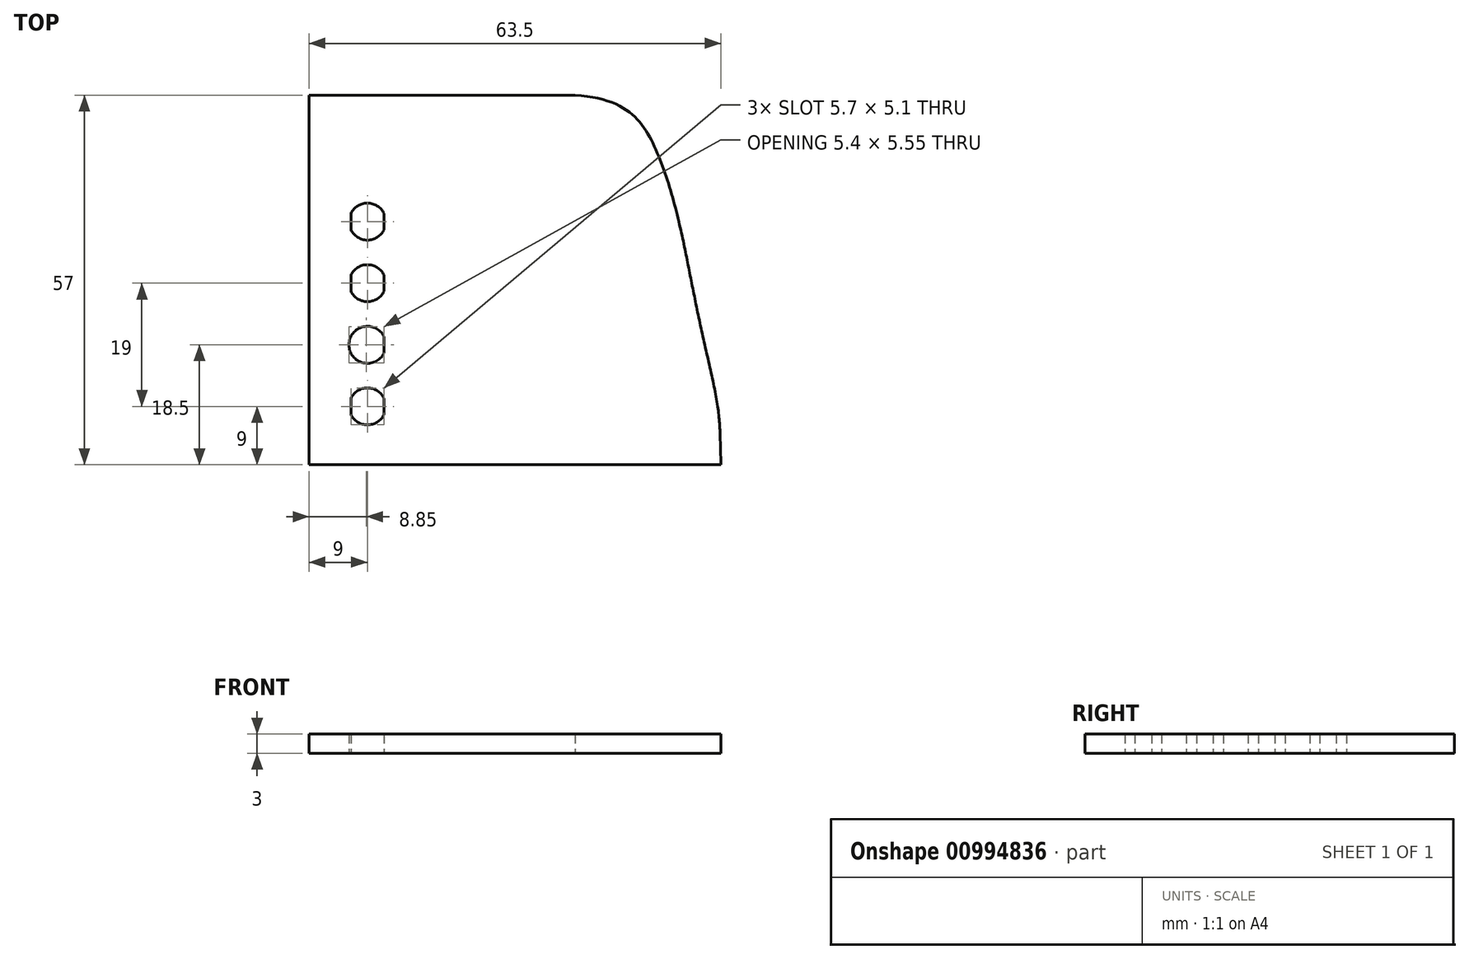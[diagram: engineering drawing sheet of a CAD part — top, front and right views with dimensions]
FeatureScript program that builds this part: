
annotation { "Feature Type Name" : "Feature", "Feature Type Description" : "" }
export const myFeature = defineFeature(function(context is Context, id is Id, definition is map)
    precondition{}
    {
        {
            var Q0;
            Q0=qCreatedBy(makeId("Top.planeOp"),FACE);
            var sketch = newSketch(context, id + "F0", { "sketchPlane" : qUnion([Q0])});
            skCircle(sketch, "E0", {"center": v(0, 0) * mm, "radius": 2.85 * mm});
            skLineSegment(sketch, "E1", {"start": v(0, 0) * mm, "end": v(0, 48) * mm, "construction": true});
            skLineSegment(sketch, "E2", {"start": v(2.55, 48) * mm, "end": v(2.55, 0) * mm});
            skLineSegment(sketch, "E3.MirrorCS", {"start": v(-2.55, 48) * mm, "end": v(-2.55, 0) * mm});
            skCircle(sketch, "E4", {"center": v(0, 9.5) * mm, "radius": 2.85 * mm});
            skCircle(sketch, "E5", {"center": v(0, 19) * mm, "radius": 2.85 * mm});
            skCircle(sketch, "E6", {"center": v(0, 28.5) * mm, "radius": 2.85 * mm});
            skLineSegment(sketch, "E7", {"start": v(0, 0) * mm, "end": v(0, -9) * mm, "construction": true});
            skLineSegment(sketch, "E8", {"start": v(0, -9) * mm, "end": v(-9, -9) * mm});
            skLineSegment(sketch, "E9", {"start": v(-9, -9) * mm, "end": v(-9, 48) * mm});
            skLineSegment(sketch, "E10", {"start": v(-9, 48) * mm, "end": v(0, 48) * mm});
            skLineSegment(sketch, "E11.MirrorCS", {"start": v(0, -9) * mm, "end": v(9, -9) * mm});
            skLineSegment(sketch, "E12.MirrorCS", {"start": v(9, 48) * mm, "end": v(0, 48) * mm});
            skLineSegment(sketch, "E13.MirrorCS", {"start": v(9, -9) * mm, "end": v(9, 48) * mm});
            skLineSegment(sketch, "E14", {"start": v(9, 48) * mm, "end": v(32, 48) * mm});
            skLineSegment(sketch, "E15", {"start": v(0, 0) * mm, "end": v(54, 0) * mm});
            skLineSegment(sketch, "E16", {"start": v(0, 19) * mm, "end": v(50, 19) * mm});
            skLineSegment(sketch, "E17", {"start": v(0, 28.5) * mm, "end": v(48, 28.5) * mm});
            skLineSegment(sketch, "E18", {"start": v(0, 9.5) * mm, "end": v(52, 9.5) * mm});
            skLineSegment(sketch, "E19", {"start": v(0, 40.6) * mm, "end": v(44, 40.6) * mm});
            skLineSegment(sketch, "E20", {"start": v(0, -9) * mm, "end": v(54.5, -9) * mm});
            skFitSpline(sketch, "E21", {"points": [v(32, 48) * mm, v(44, 40.6) * mm, v(48, 28.5) * mm, v(50, 19) * mm, v(52, 9.5) * mm, v(54, 0) * mm, v(54.5, -9) * mm], "startDerivative": vector(119.63, -8.28) * mm, "endDerivative": vector(2.44, -86.6) * mm});
            skLineSegment(sketch, "E22.MirrorCS", {"start": v(2.55, -48) * mm, "end": v(2.55, 0) * mm});
            skLineSegment(sketch, "E23.MirrorCS", {"start": v(-2.55, -48) * mm, "end": v(-2.55, 0) * mm});
            skSolve(sketch);
        }
        {
            var Q0;
            {var subQ0=sQuery(id+"F0.wireOp",EDGE,"E15");var subQ1=sQuery(id+"F0.wireOp",EDGE,"E0");var subQ2=makeQuery(id+"F0.imprint","INTERSECT",VERTEX,{"derivedFrom":[subQ1,subQ0]});Q0=makeQuery(id+"F0.imprint","IMPRINT",FACE,{"disambiguationData":[TD([[makeQuery(id+"F0.imprint","IMPRINT",EDGE,{"disambiguationData":[TD([[subQ2,1.0]])],"derivedFrom":subQ1}),-1.0]])]});}
            var Q1;
            {var subQ3=sQuery(id+"F0.wireOp",EDGE,"E0");var subQ7=sQuery(id+"F0.wireOp",EDGE,"E23.MirrorCS");var subQ9=makeQuery(id+"F0.imprint","INTERSECT",VERTEX,{"derivedFrom":[subQ3,subQ7]});Q1=makeQuery(id+"F0.imprint","IMPRINT",FACE,{"disambiguationData":[TD([[makeQuery(id+"F0.imprint","IMPRINT",EDGE,{"disambiguationData":[TD([[subQ9,-1.0]])],"derivedFrom":subQ3}),-1.0]])]});}
            var Q2;
            {var subQ0=sQuery(id+"F0.wireOp",EDGE,"E9");Q2=makeQuery(id+"F0.imprint","IMPRINT",FACE,{"disambiguationData":[TD([[makeQuery(id+"F0.imprint","IMPRINT",EDGE,{"derivedFrom":subQ0}),-1.0]])]});}
            var Q3;
            {var subQ0=sQuery(id+"F0.wireOp",EDGE,"E2");var subQ1=sQuery(id+"F0.wireOp",EDGE,"E0");var subQ2=makeQuery(id+"F0.imprint","INTERSECT",VERTEX,{"derivedFrom":[subQ1,subQ0]});Q3=makeQuery(id+"F0.imprint","IMPRINT",FACE,{"disambiguationData":[TD([[makeQuery(id+"F0.imprint","IMPRINT",EDGE,{"disambiguationData":[TD([[subQ2,-1.0]])],"derivedFrom":subQ1}),-1.0]])]});}
            var Q4;
            {var subQ0=sQuery(id+"F0.wireOp",EDGE,"E6");var subQ1=sQuery(id+"F0.wireOp",EDGE,"E2");var subQ2=makeQuery(id+"F0.imprint","INTERSECT",VERTEX,{"disambiguationData":[OD(1.0)],"derivedFrom":[subQ1,subQ0]});Q4=makeQuery(id+"F0.imprint","IMPRINT",FACE,{"disambiguationData":[TD([[makeQuery(id+"F0.imprint","IMPRINT",EDGE,{"disambiguationData":[TD([[subQ2,-1.0]])],"derivedFrom":subQ1}),-1.0]])]});}
            var Q5;
            {var subQ0=sQuery(id+"F0.wireOp",EDGE,"E5");var subQ1=sQuery(id+"F0.wireOp",EDGE,"E2");var subQ2=makeQuery(id+"F0.imprint","INTERSECT",VERTEX,{"disambiguationData":[OD(1.0)],"derivedFrom":[subQ1,subQ0]});Q5=makeQuery(id+"F0.imprint","IMPRINT",FACE,{"disambiguationData":[TD([[makeQuery(id+"F0.imprint","IMPRINT",EDGE,{"disambiguationData":[TD([[subQ2,-1.0]])],"derivedFrom":subQ1}),-1.0]])]});}
            var Q6;
            {var subQ5=sQuery(id+"F0.wireOp",EDGE,"E2");var subQ8=sQuery(id+"F0.wireOp",EDGE,"E12.MirrorCS");var subQ9=makeQuery(id+"F0.imprint","INTERSECT",VERTEX,{"derivedFrom":[subQ5,subQ8]});Q6=makeQuery(id+"F0.imprint","IMPRINT",FACE,{"disambiguationData":[TD([[makeQuery(id+"F0.imprint","IMPRINT",EDGE,{"disambiguationData":[TD([[subQ9,-1.0]])],"derivedFrom":subQ5}),-1.0]])]});}
            var Q7;
            {var subQ0=sQuery(id+"F0.wireOp",EDGE,"E18");var subQ1=sQuery(id+"F0.wireOp",EDGE,"E2");var subQ2=makeQuery(id+"F0.imprint","INTERSECT",VERTEX,{"derivedFrom":[subQ1,subQ0]});Q7=makeQuery(id+"F0.imprint","IMPRINT",FACE,{"disambiguationData":[TD([[makeQuery(id+"F0.imprint","IMPRINT",EDGE,{"disambiguationData":[TD([[subQ2,-1.0]])],"derivedFrom":subQ1}),1.0]])]});}
            var Q8;
            {var subQ0=sQuery(id+"F0.wireOp",EDGE,"E17");var subQ1=sQuery(id+"F0.wireOp",EDGE,"E2");var subQ2=makeQuery(id+"F0.imprint","INTERSECT",VERTEX,{"derivedFrom":[subQ1,subQ0]});Q8=makeQuery(id+"F0.imprint","IMPRINT",FACE,{"disambiguationData":[TD([[makeQuery(id+"F0.imprint","IMPRINT",EDGE,{"disambiguationData":[TD([[subQ2,1.0]])],"derivedFrom":subQ1}),1.0]])]});}
            var Q9;
            {var subQ0=sQuery(id+"F0.wireOp",EDGE,"E18");var subQ1=sQuery(id+"F0.wireOp",EDGE,"E2");var subQ2=makeQuery(id+"F0.imprint","INTERSECT",VERTEX,{"derivedFrom":[subQ1,subQ0]});Q9=makeQuery(id+"F0.imprint","IMPRINT",FACE,{"disambiguationData":[TD([[makeQuery(id+"F0.imprint","IMPRINT",EDGE,{"disambiguationData":[TD([[subQ2,1.0]])],"derivedFrom":subQ1}),1.0]])]});}
            var Q10;
            {var subQ0=sQuery(id+"F0.wireOp",EDGE,"E4");var subQ1=sQuery(id+"F0.wireOp",EDGE,"E3.MirrorCS");var subQ2=makeQuery(id+"F0.imprint","INTERSECT",VERTEX,{"disambiguationData":[OD(0.0)],"derivedFrom":[subQ1,subQ0]});Q10=makeQuery(id+"F0.imprint","IMPRINT",FACE,{"disambiguationData":[TD([[makeQuery(id+"F0.imprint","IMPRINT",EDGE,{"disambiguationData":[TD([[subQ2,-1.0]])],"derivedFrom":subQ1}),-1.0]])]});}
            var Q11;
            {var subQ0=sQuery(id+"F0.wireOp",EDGE,"E6");var subQ1=sQuery(id+"F0.wireOp",EDGE,"E3.MirrorCS");var subQ2=makeQuery(id+"F0.imprint","INTERSECT",VERTEX,{"disambiguationData":[OD(0.0)],"derivedFrom":[subQ1,subQ0]});Q11=makeQuery(id+"F0.imprint","IMPRINT",FACE,{"disambiguationData":[TD([[makeQuery(id+"F0.imprint","IMPRINT",EDGE,{"disambiguationData":[TD([[subQ2,-1.0]])],"derivedFrom":subQ1}),-1.0]])]});}
            var Q12;
            {var subQ0=sQuery(id+"F0.wireOp",EDGE,"E5");var subQ1=sQuery(id+"F0.wireOp",EDGE,"E3.MirrorCS");var subQ2=makeQuery(id+"F0.imprint","INTERSECT",VERTEX,{"disambiguationData":[OD(0.0)],"derivedFrom":[subQ1,subQ0]});Q12=makeQuery(id+"F0.imprint","IMPRINT",FACE,{"disambiguationData":[TD([[makeQuery(id+"F0.imprint","IMPRINT",EDGE,{"disambiguationData":[TD([[subQ2,-1.0]])],"derivedFrom":subQ1}),-1.0]])]});}
            var Q13;
            {var subQ0=sQuery(id+"F0.wireOp",EDGE,"E17");var subQ1=sQuery(id+"F0.wireOp",EDGE,"E2");var subQ2=makeQuery(id+"F0.imprint","INTERSECT",VERTEX,{"derivedFrom":[subQ1,subQ0]});Q13=makeQuery(id+"F0.imprint","IMPRINT",FACE,{"disambiguationData":[TD([[makeQuery(id+"F0.imprint","IMPRINT",EDGE,{"disambiguationData":[TD([[subQ2,-1.0]])],"derivedFrom":subQ1}),1.0]])]});}
            var Q14;
            {var subQ0=sQuery(id+"F0.wireOp",EDGE,"E16");var subQ1=sQuery(id+"F0.wireOp",EDGE,"E2");var subQ2=makeQuery(id+"F0.imprint","INTERSECT",VERTEX,{"derivedFrom":[subQ1,subQ0]});Q14=makeQuery(id+"F0.imprint","IMPRINT",FACE,{"disambiguationData":[TD([[makeQuery(id+"F0.imprint","IMPRINT",EDGE,{"disambiguationData":[TD([[subQ2,-1.0]])],"derivedFrom":subQ1}),1.0]])]});}
            var Q15;
            {var subQ0=sQuery(id+"F0.wireOp",EDGE,"E3.MirrorCS");var subQ1=sQuery(id+"F0.wireOp",EDGE,"E0");var subQ2=makeQuery(id+"F0.imprint","INTERSECT",VERTEX,{"derivedFrom":[subQ1,subQ0]});Q15=makeQuery(id+"F0.imprint","IMPRINT",FACE,{"disambiguationData":[TD([[makeQuery(id+"F0.imprint","IMPRINT",EDGE,{"disambiguationData":[TD([[subQ2,-1.0]])],"derivedFrom":subQ1}),1.0]])]});}
            var Q16;
            {var subQ0=sQuery(id+"F0.wireOp",EDGE,"E16");var subQ1=sQuery(id+"F0.wireOp",EDGE,"E2");var subQ2=makeQuery(id+"F0.imprint","INTERSECT",VERTEX,{"derivedFrom":[subQ1,subQ0]});Q16=makeQuery(id+"F0.imprint","IMPRINT",FACE,{"disambiguationData":[TD([[makeQuery(id+"F0.imprint","IMPRINT",EDGE,{"disambiguationData":[TD([[subQ2,1.0]])],"derivedFrom":subQ1}),1.0]])]});}
            var Q17;
            {var subQ0=sQuery(id+"F0.wireOp",EDGE,"E2");var subQ1=sQuery(id+"F0.wireOp",EDGE,"E0");var subQ2=makeQuery(id+"F0.imprint","INTERSECT",VERTEX,{"derivedFrom":[subQ1,subQ0]});Q17=makeQuery(id+"F0.imprint","IMPRINT",FACE,{"disambiguationData":[TD([[makeQuery(id+"F0.imprint","IMPRINT",EDGE,{"disambiguationData":[TD([[subQ2,1.0]])],"derivedFrom":subQ1}),1.0]])]});}
            var Q18;
            {var subQ0=sQuery(id+"F0.wireOp",EDGE,"E15");var subQ1=sQuery(id+"F0.wireOp",EDGE,"E0");var subQ2=makeQuery(id+"F0.imprint","INTERSECT",VERTEX,{"derivedFrom":[subQ1,subQ0]});Q18=makeQuery(id+"F0.imprint","IMPRINT",FACE,{"disambiguationData":[TD([[makeQuery(id+"F0.imprint","IMPRINT",EDGE,{"disambiguationData":[TD([[subQ2,1.0]])],"derivedFrom":subQ1}),1.0]])]});}
            var Q19;
            {var subQ5=sQuery(id+"F0.wireOp",EDGE,"E5");var subQ6=sQuery(id+"F0.wireOp",EDGE,"E2");var subQ7=makeQuery(id+"F0.imprint","INTERSECT",VERTEX,{"disambiguationData":[OD(1.0)],"derivedFrom":[subQ6,subQ5]});Q19=makeQuery(id+"F0.imprint","IMPRINT",FACE,{"disambiguationData":[TD([[makeQuery(id+"F0.imprint","IMPRINT",EDGE,{"disambiguationData":[TD([[subQ7,-1.0]])],"derivedFrom":subQ6}),1.0]])]});}
            var Q20;
            {var subQ5=sQuery(id+"F0.wireOp",EDGE,"E2");var subQ6=sQuery(id+"F0.wireOp",EDGE,"E0");var subQ7=makeQuery(id+"F0.imprint","INTERSECT",VERTEX,{"derivedFrom":[subQ6,subQ5]});Q20=makeQuery(id+"F0.imprint","IMPRINT",FACE,{"disambiguationData":[TD([[makeQuery(id+"F0.imprint","IMPRINT",EDGE,{"disambiguationData":[TD([[subQ7,1.0]])],"derivedFrom":subQ6}),-1.0]])]});}
            var Q21;
            {var subQ1=sQuery(id+"F0.wireOp",EDGE,"E2");var subQ7=sQuery(id+"F0.wireOp",EDGE,"E19");var subQ8=makeQuery(id+"F0.imprint","INTERSECT",VERTEX,{"derivedFrom":[subQ1,subQ7]});Q21=makeQuery(id+"F0.imprint","IMPRINT",FACE,{"disambiguationData":[TD([[makeQuery(id+"F0.imprint","IMPRINT",EDGE,{"disambiguationData":[TD([[subQ8,-1.0]])],"derivedFrom":subQ1}),1.0]])]});}
            var Q22;
            {var subQ5=sQuery(id+"F0.wireOp",EDGE,"E6");var subQ6=sQuery(id+"F0.wireOp",EDGE,"E2");var subQ7=makeQuery(id+"F0.imprint","INTERSECT",VERTEX,{"disambiguationData":[OD(1.0)],"derivedFrom":[subQ6,subQ5]});Q22=makeQuery(id+"F0.imprint","IMPRINT",FACE,{"disambiguationData":[TD([[makeQuery(id+"F0.imprint","IMPRINT",EDGE,{"disambiguationData":[TD([[subQ7,-1.0]])],"derivedFrom":subQ6}),1.0]])]});}
            var Q23;
            {var subQ0=sQuery(id+"F0.wireOp",EDGE,"E12.MirrorCS");var subQ1=sQuery(id+"F0.wireOp",EDGE,"E2");var subQ2=makeQuery(id+"F0.imprint","INTERSECT",VERTEX,{"derivedFrom":[subQ1,subQ0]});Q23=makeQuery(id+"F0.imprint","IMPRINT",FACE,{"disambiguationData":[TD([[makeQuery(id+"F0.imprint","IMPRINT",EDGE,{"disambiguationData":[TD([[subQ2,-1.0]])],"derivedFrom":subQ1}),1.0]])]});}
            var Q24;
            {var subQ0=sQuery(id+"F0.wireOp",EDGE,"E18");var subQ1=sQuery(id+"F0.wireOp",EDGE,"E13.MirrorCS");var subQ2=makeQuery(id+"F0.imprint","INTERSECT",VERTEX,{"derivedFrom":[subQ1,subQ0]});Q24=makeQuery(id+"F0.imprint","IMPRINT",FACE,{"disambiguationData":[TD([[makeQuery(id+"F0.imprint","IMPRINT",EDGE,{"disambiguationData":[TD([[subQ2,-1.0]])],"derivedFrom":subQ1}),-1.0]])]});}
            var Q25;
            {var subQ0=sQuery(id+"F0.wireOp",EDGE,"E16");var subQ1=sQuery(id+"F0.wireOp",EDGE,"E13.MirrorCS");var subQ2=makeQuery(id+"F0.imprint","INTERSECT",VERTEX,{"derivedFrom":[subQ1,subQ0]});Q25=makeQuery(id+"F0.imprint","IMPRINT",FACE,{"disambiguationData":[TD([[makeQuery(id+"F0.imprint","IMPRINT",EDGE,{"disambiguationData":[TD([[subQ2,-1.0]])],"derivedFrom":subQ1}),-1.0]])]});}
            var Q26;
            {var subQ0=sQuery(id+"F0.wireOp",EDGE,"E17");var subQ1=sQuery(id+"F0.wireOp",EDGE,"E13.MirrorCS");var subQ2=makeQuery(id+"F0.imprint","INTERSECT",VERTEX,{"derivedFrom":[subQ1,subQ0]});Q26=makeQuery(id+"F0.imprint","IMPRINT",FACE,{"disambiguationData":[TD([[makeQuery(id+"F0.imprint","IMPRINT",EDGE,{"disambiguationData":[TD([[subQ2,-1.0]])],"derivedFrom":subQ1}),-1.0]])]});}
            var Q27;
            {var subQ0=sQuery(id+"F0.wireOp",EDGE,"E14");Q27=makeQuery(id+"F0.imprint","IMPRINT",FACE,{"disambiguationData":[TD([[makeQuery(id+"F0.imprint","IMPRINT",EDGE,{"derivedFrom":subQ0}),-1.0]])]});}
            var Q28;
            {var subQ0=sQuery(id+"F0.wireOp",EDGE,"E15");var subQ1=sQuery(id+"F0.wireOp",EDGE,"E13.MirrorCS");var subQ2=makeQuery(id+"F0.imprint","INTERSECT",VERTEX,{"derivedFrom":[subQ1,subQ0]});Q28=makeQuery(id+"F0.imprint","IMPRINT",FACE,{"disambiguationData":[TD([[makeQuery(id+"F0.imprint","IMPRINT",EDGE,{"disambiguationData":[TD([[subQ2,-1.0]])],"derivedFrom":subQ1}),-1.0]])]});}
            var Q29;
            {var subQ0=sQuery(id+"F0.wireOp",EDGE,"E20");var subQ1=sQuery(id+"F0.wireOp",EDGE,"E13.MirrorCS");var subQ2=makeQuery(id+"F0.imprint","INTERSECT",VERTEX,{"derivedFrom":[subQ1,subQ0]});Q29=makeQuery(id+"F0.imprint","IMPRINT",FACE,{"disambiguationData":[TD([[makeQuery(id+"F0.imprint","IMPRINT",EDGE,{"disambiguationData":[TD([[subQ2,-1.0]])],"derivedFrom":subQ1}),-1.0]])]});}
            extrude(context, id + "F1", {"entities" : qUnion([Q0, Q1, Q2, Q3, Q4, Q5, Q6, Q7, Q8, Q9, Q10, Q11, Q12, Q13, Q14, Q15, Q16, Q17, Q18, Q19, Q20, Q21, Q22, Q23, Q24, Q25, Q26, Q27, Q28, Q29]), "depth" : 3 * mm, "offsetDistance" : 25 * mm});
        }
    });
